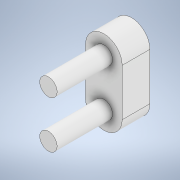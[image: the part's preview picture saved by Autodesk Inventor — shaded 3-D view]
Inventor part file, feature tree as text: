
AUTODESK INVENTOR PART (.ipt)
format: ipt  version: 2022 (Build 260153000, 153)  size: 121,856 bytes
history: native  units: in
note: dims shown in document units (in); Inventor stores cm internally (conversion verified against a paired STEP export)
features: extrude x2, sketch x2, other x1
ambient origin geometry x8: Origin, YZ Plane, XZ Plane, XY Plane, X Axis, Y Axis, Z Axis, Center Point
bodies: Body1 (feature_tree)
feature tree (5):
  other  "Sólido1"
  extrude  "Extrusión1"  Depth=0.0984in
  extrude  "Extrusión2"  Depth=0.4724in TaperAngle=0.0deg
  sketch  "Boceto1"  dims[d0=0.0984in d1=0.0984in]
  sketch  "Boceto2"  dims[d2=0.1575in d3=0.0in d4=0.4724in d5=0.0in d6=0.1039in d7=0.1039in d8=0.2677in d9=0.2077in]
